# Revit family: WCPan-RimEx-WallHung-54cm-Vitra-İntegraSeries-7082
name_source: partatom
category: Plumbing Fixtures
revit_build: Autodesk Revit 2017 (Build: 20160225_1515(x64)
units: mm (PartAtom-declared; Revit-internal decimal feet)

## family parameters
Cut with Voids When Loaded = No
Host = Face
OmniClass Number = 23.45.05.21.11
OmniClass Title = Water Closets
Part Type = Normal
Room Calculation Point = No
Round Connector Dimension = Use Diameter
Shared = Yes

## types (4) — shared parameters
BIMobject category = Sanitary - Toilets
Brand = VitrA
CW Connection = Yes
Color = White
Default Elevation = 410 mm  [stored 1.34514 ft]
Design country = Turkey
IFC Classification = Sanitary Terminal
Main Material = Ceramic
Manufacturer = Vitra
Manufacturer name = Vitra
Masterformat 2014 Code = 22 45 26
Masterformat 2014 Description = Sanitary Facilities
Mounting type = Wall Hung
NBS Referans Code = 35-65-90
NBS Referans Description = Toilet Systems
Nominal Depth (mm) = 545 mm  [stored 1.78806 ft]
Nominal Height (mm) = 350 mm  [stored 1.14829 ft]
Nominal Width (mm) = 365 mm  [stored 1.19751 ft]
OmniClass Code = 23-31 19 00
OmniClass Description = Toilets
Primary Material = White
Product certification = https://www.vitraglobal.com
Product family = İntegra
Product group = Wall Mounted WC
Product url = https://www.vitraglobal.com
Secondary Material = Chrome
Technical description = https://www.vitraglobal.com
UNSPSC Description = Sanitary Ware
URL = https://www.vitra.com.tr
Uniclass 1.4 Code = L7216
Uniclass 1.4 Description = Toilets
Uniclass 2.0 Code = SS-35-65-90
Uniclass 2.0 Description = Toilet Systems
Uniclass 2015 Code = Pr_40_20_93
Uniclass 2015 Name = Urinal and WC fittings
Uniformat II Code = D2010
Uniformat II Description = Sanitary Facilities
Vent Connection = No
Warranty Period (Year) = 10 Years
Waste Connection = Yes
Youtube = https://www.youtube.com

## per-type parameters (varying)
| type | Article No. (default) | Bidet pipe inlet | Description | HW Connection | Integrated Bidet Valve | Integrated Thermostatic Bidet Valve, | Model | Product SKU |
| WCPan-RimEx-WallHung-54cm-WithBidetPipeInlet-Vitra-İntegraSeries-7082B003-0090 | 7082B003-0090 | Yes | VitrA Integra Wall-Hung - 54cm - With Bidet Pipe Inlet | No | No | No | 7082B003-0090 | 7082B003-0090 |
| WCPan-RimEx-WallHung-54cm-WithoutBidetPipeInlet-Vitra-İntegraSeries-7082B003-0075 | 7082B003-0075 | No | VitrA Integra Wall-Hung - 54cm - Without Bidet Pipe Inlet | No | No | No | 7082B003-0075 | 7082B003-0075 |
| WCPan-RimEx-WallHung-54cm-WithBidetPipeInlet-Vitra-İntegraSeries-7082B003-7209 | 7082B003-7209 | Yes | VitrA Integra Wall-Hung - 54cm - With Bidet Pipe Inlet | Yes | Yes | No | 7082B003-7209 | 7082B003-7209 |
| WCPan-RimEx-WallHung-54cm-WithBidetPipeInlet-Vitra-İntegraSeries-7082B003-7211 | 7082B003-7211 | Yes | VitrA Integra Wall-Hung - 54cm - With Bidet Pipe Inlet | Yes | No | Yes | 7082B003-7211 | 7082B003-7211 |

note: [stored X ft] marks values corroborated as IEEE doubles in the binary element streams (Revit-internal decimal feet)

## geometry (parser evidence)
native form markers: Sweep x2
no freeform markers — native parametric forms only
